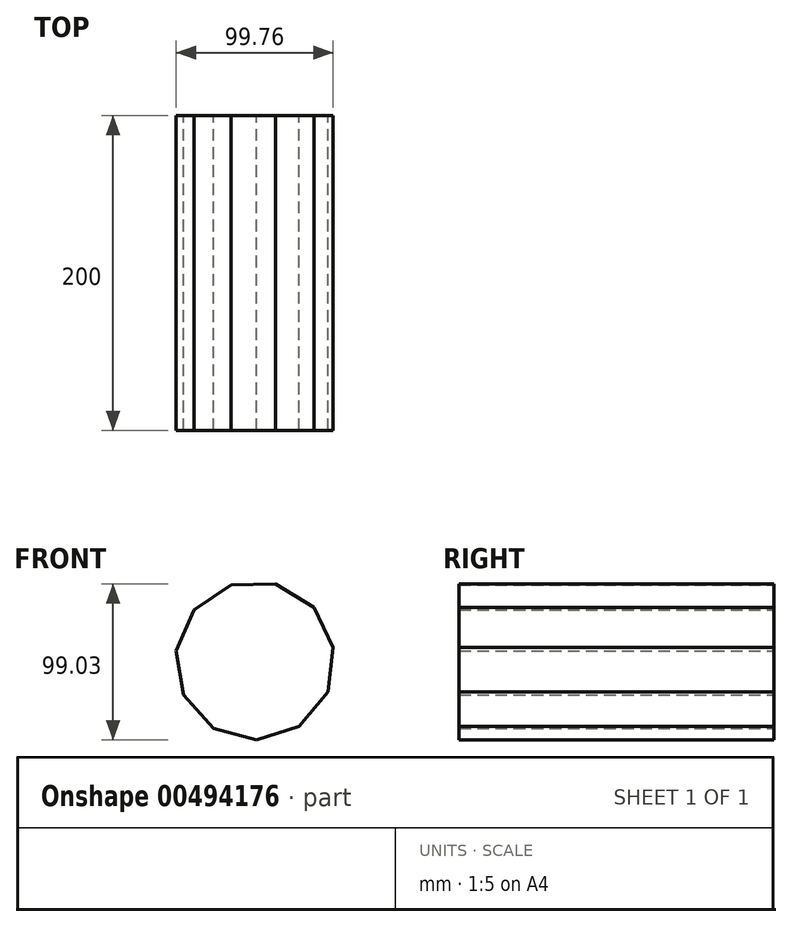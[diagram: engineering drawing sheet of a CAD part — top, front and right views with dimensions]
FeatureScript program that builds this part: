
annotation { "Feature Type Name" : "Feature", "Feature Type Description" : "" }
export const myFeature = defineFeature(function(context is Context, id is Id, definition is map)
    precondition{}
    {
        {
            var Q0;
            Q0=qCreatedBy(makeId("Front.planeOp"),FACE);
            var sketch = newSketch(context, id + "F0", { "sketchPlane" : qUnion([Q0])});
            skCircle(sketch, "E0.cCircle", {"center": v(0, 0) * mm, "radius": 50.4 * mm, "construction": true});
            skLineSegment(sketch, "E0.0", {"start": v(-38.77, 32.2) * mm, "end": v(-15.2, 48.05) * mm});
            skLineSegment(sketch, "E0.1", {"start": v(-15.2, 48.05) * mm, "end": v(13.2, 48.64) * mm});
            skLineSegment(sketch, "E0.2", {"start": v(13.2, 48.64) * mm, "end": v(37.4, 33.79) * mm});
            skLineSegment(sketch, "E0.3", {"start": v(37.4, 33.79) * mm, "end": v(49.73, 8.2) * mm});
            skLineSegment(sketch, "E0.4", {"start": v(49.73, 8.2) * mm, "end": v(46.27, -19.98) * mm});
            skLineSegment(sketch, "E0.5", {"start": v(46.27, -19.98) * mm, "end": v(28.12, -41.83) * mm});
            skLineSegment(sketch, "E0.6", {"start": v(28.12, -41.83) * mm, "end": v(1.05, -50.39) * mm});
            skLineSegment(sketch, "E0.7", {"start": v(1.05, -50.39) * mm, "end": v(-26.36, -42.96) * mm});
            skLineSegment(sketch, "E0.8", {"start": v(-26.36, -42.96) * mm, "end": v(-45.4, -21.88) * mm});
            skLineSegment(sketch, "E0.9", {"start": v(-45.4, -21.88) * mm, "end": v(-50.03, 6.14) * mm});
            skLineSegment(sketch, "E0.10", {"start": v(-50.03, 6.14) * mm, "end": v(-38.77, 32.2) * mm});
            skSolve(sketch);
        }
        {
            var Q0;
            Q0=makeQuery(id+"F0.imprint","IMPRINT",FACE,{"disambiguationData":[TD([[makeQuery(id+"F0.imprint","IMPRINT",EDGE,{"derivedFrom":sQuery(id+"F0.wireOp",EDGE,"E0.0")}),-1.0]])]});
            extrude(context, id + "F1", {"entities" : qUnion([Q0]), "endBound" : BoundingType.SYMMETRIC, "depth" : 200 * mm});
        }
    });
